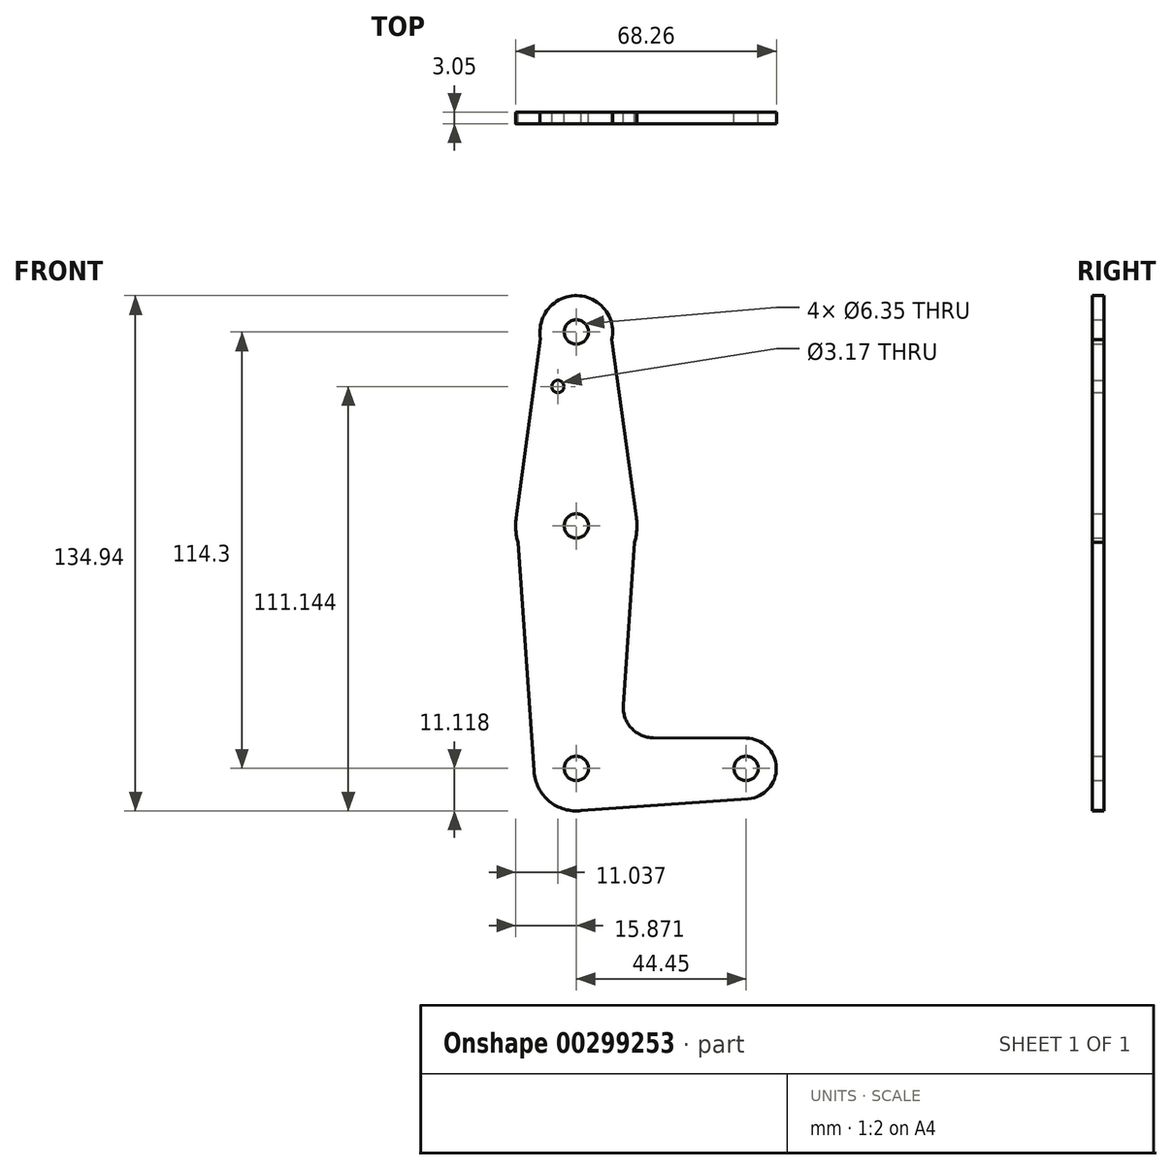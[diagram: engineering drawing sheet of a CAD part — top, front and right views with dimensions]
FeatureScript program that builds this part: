
annotation { "Feature Type Name" : "Feature", "Feature Type Description" : "" }
export const myFeature = defineFeature(function(context is Context, id is Id, definition is map)
    precondition{}
    {
        {
            var Q0;
            Q0=qCreatedBy(makeId("Front.planeOp"),FACE);
            var sketch = newSketch(context, id + "F0", { "sketchPlane" : qUnion([Q0])});
            skCircle(sketch, "E0", {"center": v(-30.27, -19.2) * mm, "radius": 11.12 * mm});
            skCircle(sketch, "E1", {"center": v(14.18, -19.2) * mm, "radius": 7.94 * mm});
            skCircle(sketch, "E2", {"center": v(-30.27, 44.3) * mm, "radius": 15.88 * mm});
            skCircle(sketch, "E3", {"center": v(-30.27, 95.1) * mm, "radius": 9.53 * mm});
            skLineSegment(sketch, "E4", {"start": v(-30.27, -19.2) * mm, "end": v(-30.27, 44.3) * mm, "construction": true});
            skLineSegment(sketch, "E5", {"start": v(-30.27, 44.3) * mm, "end": v(-30.27, 95.1) * mm, "construction": true});
            skLineSegment(sketch, "E6", {"start": v(-30.27, -19.2) * mm, "end": v(14.18, -19.2) * mm, "construction": true});
            skLineSegment(sketch, "E7", {"start": v(-39.64, 93.4) * mm, "end": v(-46, 46.44) * mm});
            skLineSegment(sketch, "E8", {"start": v(-46, 46.44) * mm, "end": v(-41.36, -19.97) * mm});
            skLineSegment(sketch, "E9", {"start": v(-20.96, 93.1) * mm, "end": v(-14.54, 46.47) * mm});
            skLineSegment(sketch, "E10", {"start": v(-14.54, 46.47) * mm, "end": v(-17.97, -2.65) * mm});
            skLineSegment(sketch, "E11", {"start": v(-10.07, -11.15) * mm, "end": v(14.21, -11.25) * mm});
            skLineSegment(sketch, "E12", {"start": v(-30, -30.31) * mm, "end": v(14.75, -27.1) * mm});
            skArc(sketch, "E13.filletArc", {"start": v(-17.97, -2.65) * mm, "mid": v(-15.86, -8.61) * mm, "end": v(-10.07, -11.15) * mm});
            skCircle(sketch, "E14", {"center": v(-30.27, 95.1) * mm, "radius": 3.18 * mm});
            skCircle(sketch, "E15", {"center": v(-30.27, 44.3) * mm, "radius": 3.18 * mm});
            skCircle(sketch, "E16", {"center": v(-30.27, -19.2) * mm, "radius": 3.18 * mm});
            skCircle(sketch, "E17", {"center": v(14.18, -19.2) * mm, "radius": 3.18 * mm});
            skCircle(sketch, "E18", {"center": v(-35.1, 80.83) * mm, "radius": 1.59 * mm});
            skSolve(sketch);
        }
        {
            var Q0;
            Q0 = qSketchRegion(id + "F0", true);
            extrude(context, id + "F1", {"entities" : qUnion([Q0]), "depth" : 3.05 * mm});
        }
    });
